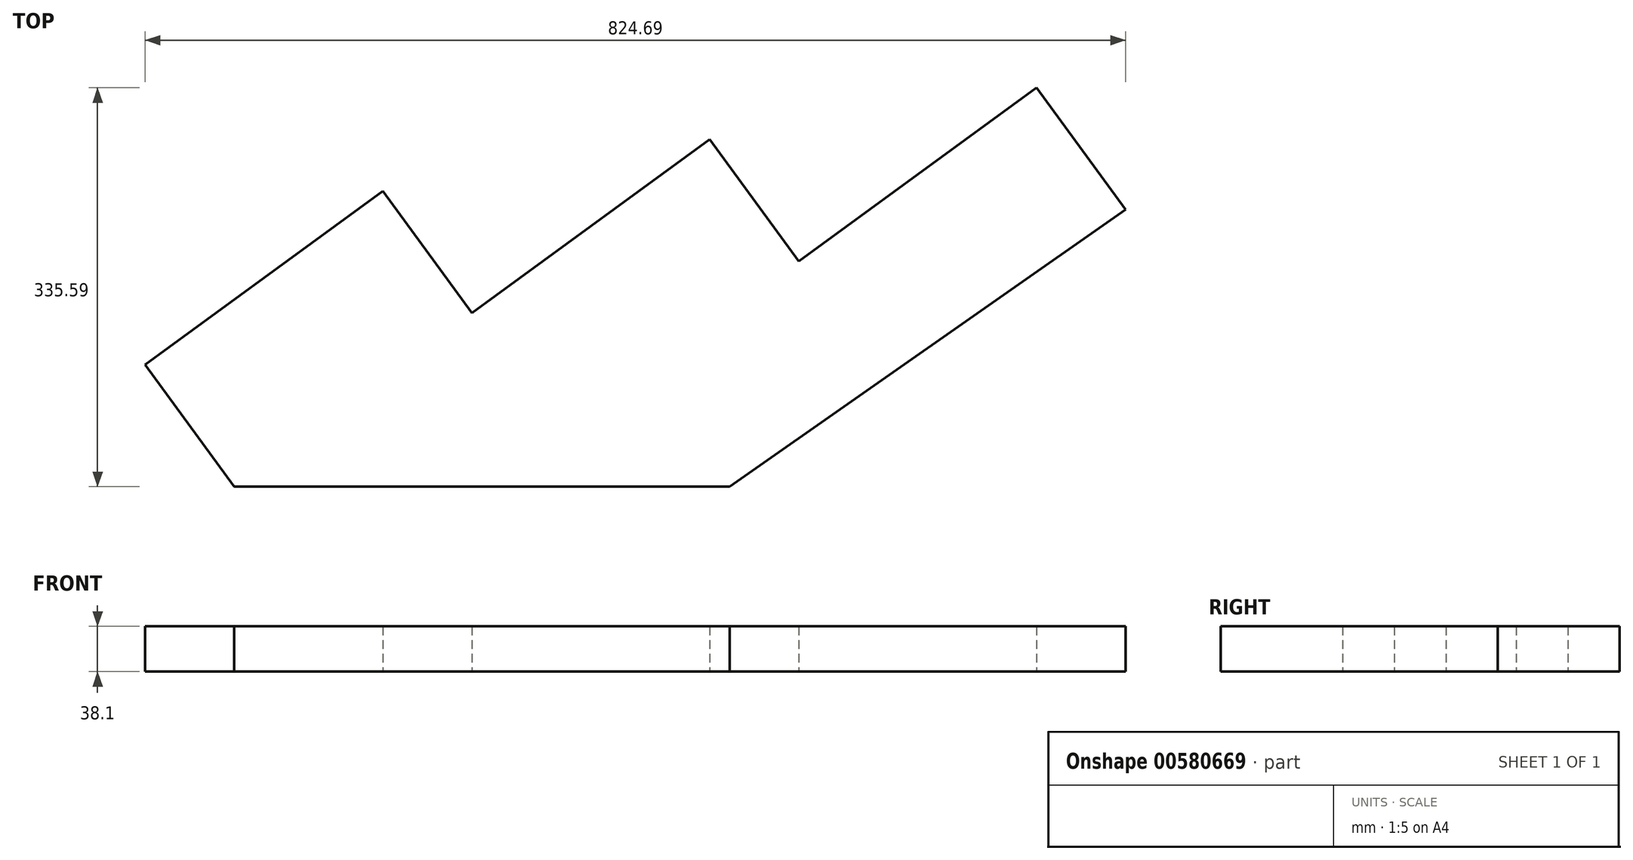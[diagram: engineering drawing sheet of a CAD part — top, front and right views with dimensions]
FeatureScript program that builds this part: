
annotation { "Feature Type Name" : "Feature", "Feature Type Description" : "" }
export const myFeature = defineFeature(function(context is Context, id is Id, definition is map)
    precondition{}
    {
        {
            var Q0;
            Q0=qCreatedBy(makeId("Top.planeOp"),FACE);
            var sketch = newSketch(context, id + "F0", { "sketchPlane" : qUnion([Q0])});
            skLineSegment(sketch, "E0.bottom", {"start": v(1524, -146.05) * mm, "end": v(-1524, -146.05) * mm, "construction": true});
            skLineSegment(sketch, "E0.top", {"start": v(1524, 146.05) * mm, "end": v(-1524, 146.05) * mm, "construction": true});
            skLineSegment(sketch, "E0.left", {"start": v(1524, -146.05) * mm, "end": v(1524, 146.05) * mm, "construction": true});
            skLineSegment(sketch, "E0.right", {"start": v(-1524, -146.05) * mm, "end": v(-1524, 146.05) * mm, "construction": true});
            skPoint(sketch, "E0.middle", {"position": v(0, 0) * mm});
            skLineSegment(sketch, "E1", {"start": v(-1292.24, 102.56) * mm, "end": v(-1217.35, 0) * mm});
            skLineSegment(sketch, "E2", {"start": v(-1217.35, 0) * mm, "end": v(-1017.35, 146.05) * mm});
            skLineSegment(sketch, "E3", {"start": v(-1017.35, 146.05) * mm, "end": v(-942.45, 43.49) * mm});
            skLineSegment(sketch, "E4", {"start": v(-710.7, 146.05) * mm, "end": v(-667.55, 86.97) * mm});
            skLineSegment(sketch, "E5", {"start": v(-1492.24, -43.49) * mm, "end": v(-1417.35, -146.05) * mm});
            skLineSegment(sketch, "E6", {"start": v(-1417.35, -146.05) * mm, "end": v(-583.78, -146.05) * mm});
            skLineSegment(sketch, "E7", {"start": v(-1217.35, 0) * mm, "end": v(-1292.24, 102.56) * mm});
            skLineSegment(sketch, "E8", {"start": v(-1292.24, 102.56) * mm, "end": v(-1492.24, -43.49) * mm});
            skPoint(sketch, "E9.start.orphan", {"position": v(-1324, 146.05) * mm});
            skLineSegment(sketch, "E10", {"start": v(-942.45, 43.49) * mm, "end": v(-742.45, 189.54) * mm});
            skLineSegment(sketch, "E11", {"start": v(-710.7, 146.05) * mm, "end": v(-742.45, 189.54) * mm});
            skPoint(sketch, "E12.orphan", {"position": v(-910.7, 0) * mm});
            skLineSegment(sketch, "E13", {"start": v(-667.55, 86.97) * mm, "end": v(-1000.56, -146.05) * mm});
            skSolve(sketch);
        }
        {
            var Q0;
            Q0=makeQuery(id+"F0.imprint","IMPRINT",FACE,{"disambiguationData":[TD([[makeQuery(id+"F0.imprint","IMPRINT",EDGE,{"derivedFrom":sQuery(id+"F0.wireOp",EDGE,"E1")}),-1.0]])]});
            extrude(context, id + "F1", {"entities" : qUnion([Q0]), "depth" : 38.1 * mm, "offsetDistance" : 25.4 * mm});
        }
        {
            var Q0;
            Q0=makeQuery(id+"F0.imprint","IMPRINT",FACE,{"disambiguationData":[TD([[makeQuery(id+"F0.imprint","IMPRINT",EDGE,{"derivedFrom":sQuery(id+"F0.wireOp",EDGE,"E2")}),-1.0]])]});
            extrude(context, id + "F2", {"entities" : qUnion([Q0]), "depth" : 38.1 * mm, "offsetDistance" : 25.4 * mm});
        }
    });
